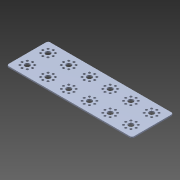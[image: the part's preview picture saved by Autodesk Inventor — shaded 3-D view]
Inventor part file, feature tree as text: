
AUTODESK INVENTOR PART (.ipt)
format: ipt  version: 2012 (Build 160160000, 160)  size: 230,400 bytes
history: native  units: in
note: dims shown in document units (in); Inventor stores cm internally (conversion verified against a paired STEP export)
features: other x2, fillet x1, imported_body x1
ambient origin geometry x8: Origin, YZ Plane, XZ Plane, XY Plane, X Axis, Y Axis, Z Axis, Center Point
feature tree (4):
  other  "Flat Plate"
  other  "Flat Plate1"
  fillet  "Fillet1"  Radius=0.125in
  imported_body  "Base1"
